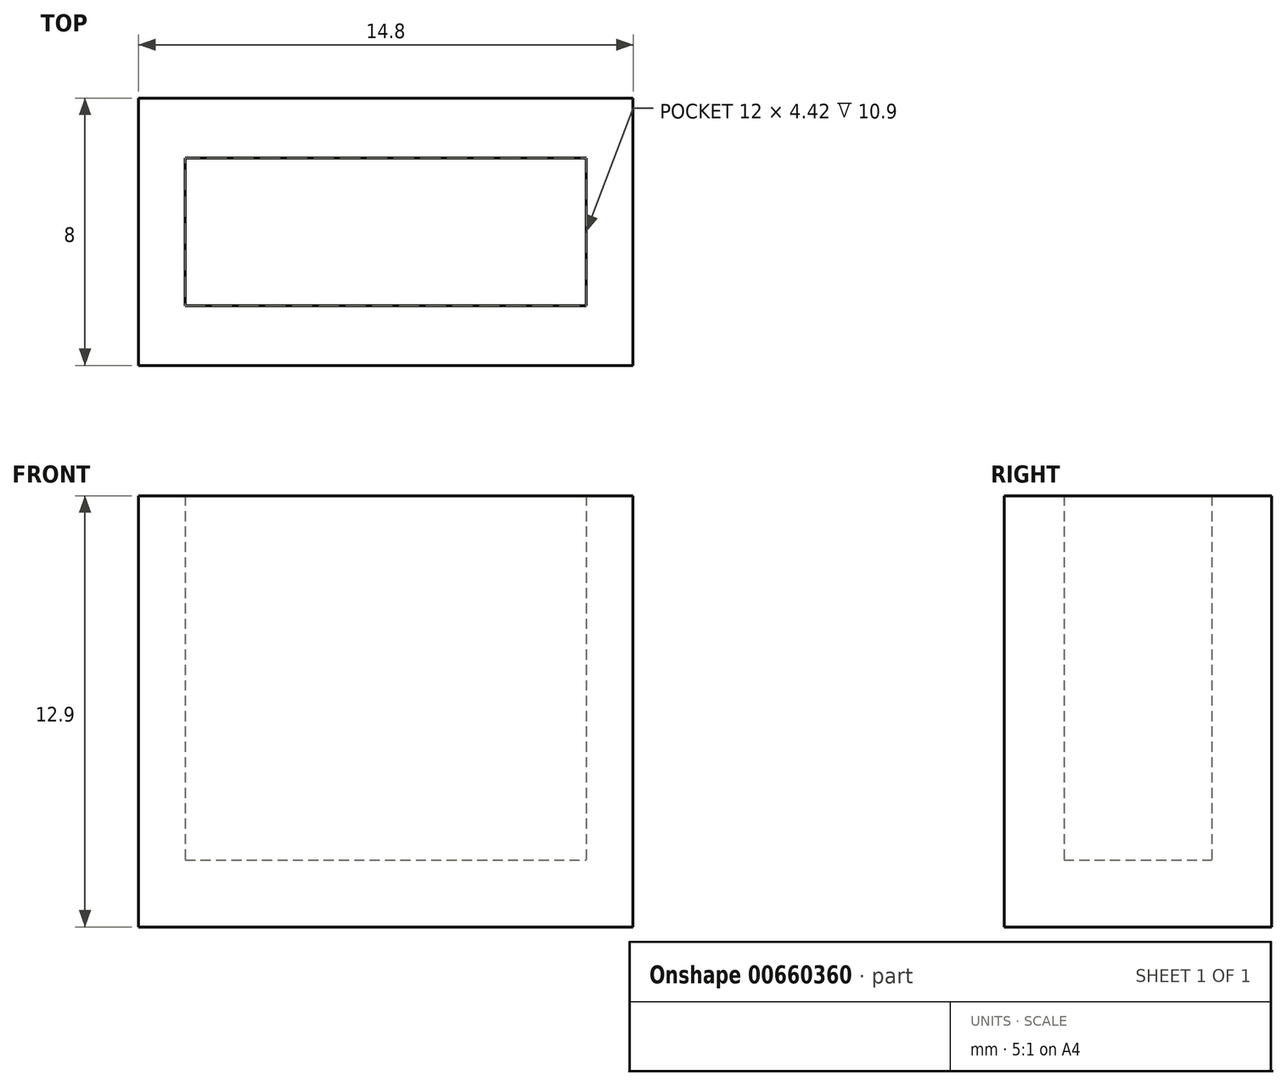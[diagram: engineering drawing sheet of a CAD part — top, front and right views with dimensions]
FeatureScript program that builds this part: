
annotation { "Feature Type Name" : "Feature", "Feature Type Description" : "" }
export const myFeature = defineFeature(function(context is Context, id is Id, definition is map)
    precondition{}
    {
        {
            var Q0;
            Q0=qCreatedBy(makeId("Top.planeOp"),FACE);
            var sketch = newSketch(context, id + "F0", { "sketchPlane" : qUnion([Q0])});
            skLineSegment(sketch, "E0.bottom", {"start": v(-15.84, 8.23) * mm, "end": v(-1.04, 8.23) * mm});
            skLineSegment(sketch, "E0.top", {"start": v(-15.84, 0.23) * mm, "end": v(-1.04, 0.23) * mm});
            skLineSegment(sketch, "E0.left", {"start": v(-15.84, 8.23) * mm, "end": v(-15.84, 0.23) * mm});
            skLineSegment(sketch, "E0.right", {"start": v(-1.04, 8.23) * mm, "end": v(-1.04, 0.23) * mm});
            skPoint(sketch, "E1", {"position": v(-14.44, 0.23) * mm});
            skPoint(sketch, "E2", {"position": v(-2.44, 0.23) * mm});
            skPoint(sketch, "E3", {"position": v(-15.84, 2.02) * mm});
            skPoint(sketch, "E4", {"position": v(-15.84, 6.44) * mm});
            skLineSegment(sketch, "E5", {"start": v(-14.44, 2.02) * mm, "end": v(-14.44, 6.44) * mm});
            skLineSegment(sketch, "E6", {"start": v(-2.44, 2.02) * mm, "end": v(-2.44, 6.44) * mm});
            skLineSegment(sketch, "E7", {"start": v(-14.44, 6.44) * mm, "end": v(-2.44, 6.44) * mm});
            skLineSegment(sketch, "E8", {"start": v(-14.44, 2.02) * mm, "end": v(-2.44, 2.02) * mm});
            skPoint(sketch, "E9.orphan", {"position": v(-2.44, 8.23) * mm});
            skPoint(sketch, "E10.orphan", {"position": v(-14.44, 8.23) * mm});
            skSolve(sketch);
        }
        {
            var Q0;
            Q0=makeQuery(id+"F0.imprint","IMPRINT",FACE,{"disambiguationData":[TD([[makeQuery(id+"F0.imprint","IMPRINT",EDGE,{"derivedFrom":sQuery(id+"F0.wireOp",EDGE,"E5")}),-1.0]])]});
            extrude(context, id + "F1", {"entities" : qUnion([Q0]), "depth" : 2 * mm, "offsetDistance" : 25 * mm});
        }
        {
            var Q0;
            Q0=qSketchRegion(id+"F0",true);
            extrude(context, id + "F2", {"entities" : qUnion([Q0]), "operationType" : NewBodyOperationType.ADD, "depth" : 12.9 * mm, "offsetDistance" : 25 * mm});
        }
    });
